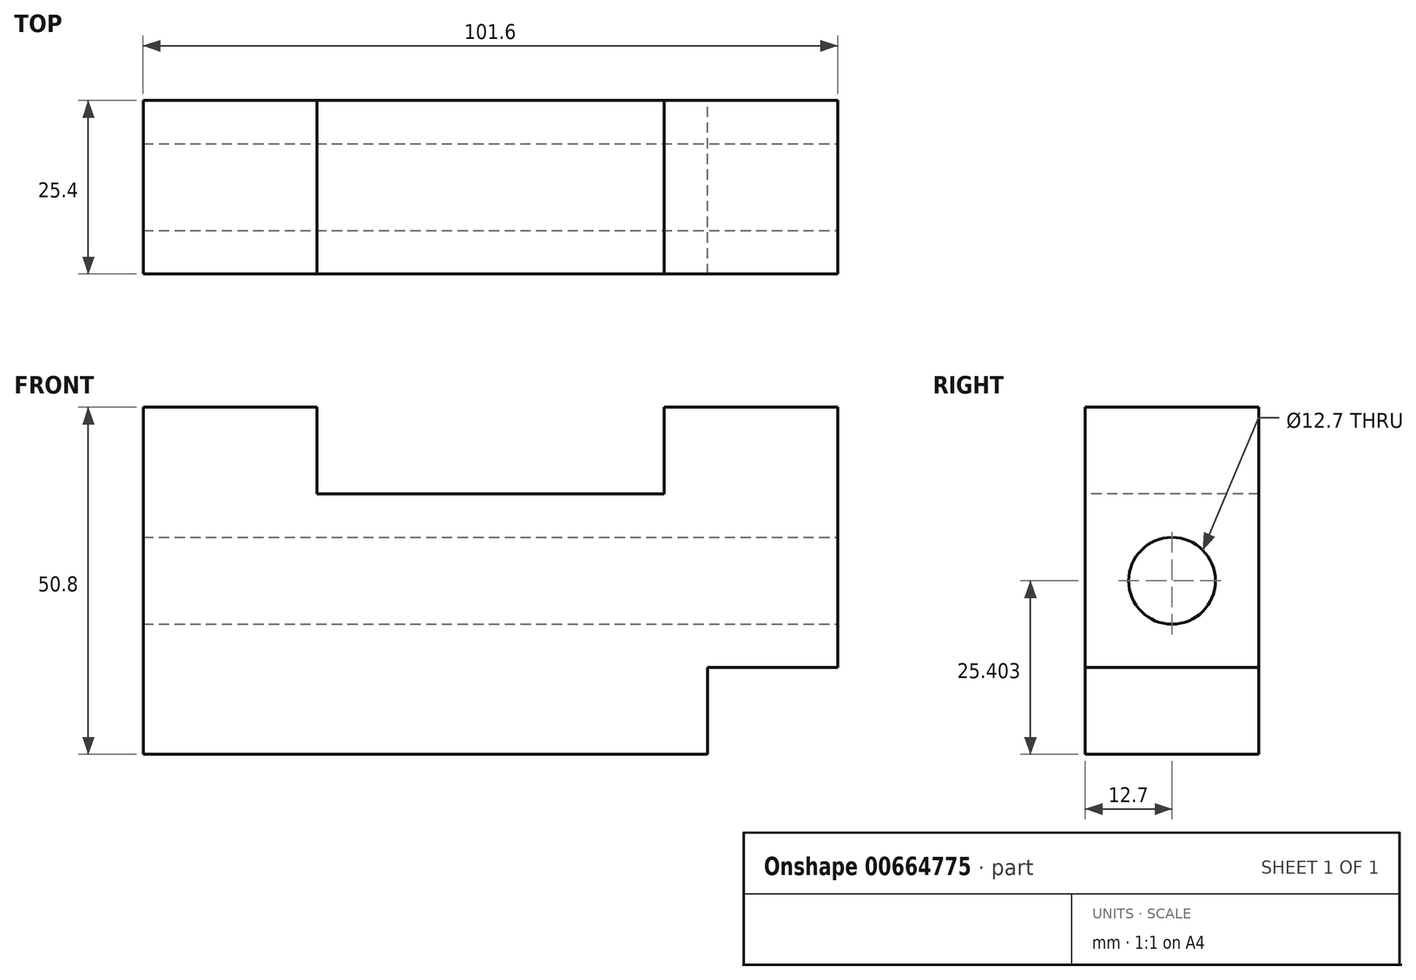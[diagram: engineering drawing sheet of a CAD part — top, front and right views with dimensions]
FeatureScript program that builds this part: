
annotation { "Feature Type Name" : "Feature", "Feature Type Description" : "" }
export const myFeature = defineFeature(function(context is Context, id is Id, definition is map)
    precondition{}
    {
        {
            var Q0;
            Q0=qCreatedBy(makeId("Front.planeOp"),FACE);
            var sketch = newSketch(context, id + "F0", { "sketchPlane" : qUnion([Q0])});
            skLineSegment(sketch, "E0.bottom", {"start": v(-52.56, 56.98) * mm, "end": v(49.04, 56.98) * mm});
            skLineSegment(sketch, "E0.top", {"start": v(-52.56, 6.18) * mm, "end": v(49.04, 6.18) * mm});
            skLineSegment(sketch, "E0.left", {"start": v(-52.56, 56.98) * mm, "end": v(-52.56, 6.18) * mm});
            skLineSegment(sketch, "E0.right", {"start": v(49.04, 56.98) * mm, "end": v(49.04, 6.18) * mm});
            skSolve(sketch);
        }
        {
            var Q0;
            Q0=makeQuery(id+"F0.imprint","IMPRINT",FACE,{"disambiguationData":[TD([[makeQuery(id+"F0.imprint","IMPRINT",EDGE,{"derivedFrom":sQuery(id+"F0.wireOp",EDGE,"E0.bottom")}),-1.0]])]});
            extrude(context, id + "F1", {"entities" : qUnion([Q0]), "depth" : 25.4 * mm, "offsetDistance" : 25.4 * mm});
        }
        {
            var Q0;
            Q0=makeQuery(id+"F1.opExtrude","CAP_FACE",FACE,{"disambiguationData":[OSD([sQuery(id+"F0.wireOp",EDGE,"E0.bottom"),sQuery(id+"F0.wireOp",EDGE,"E0.top"),sQuery(id+"F0.wireOp",EDGE,"E0.left"),sQuery(id+"F0.wireOp",EDGE,"E0.right")])],"isStart":false});
            var sketch = newSketch(context, id + "F2", { "sketchPlane" : qUnion([Q0])});
            skLineSegment(sketch, "E1.bottom", {"start": v(-27.16, 56.98) * mm, "end": v(23.64, 56.98) * mm});
            skLineSegment(sketch, "E1.top", {"start": v(-27.16, 44.28) * mm, "end": v(23.64, 44.28) * mm});
            skLineSegment(sketch, "E1.left", {"start": v(-27.16, 56.98) * mm, "end": v(-27.16, 44.28) * mm});
            skLineSegment(sketch, "E1.right", {"start": v(23.64, 56.98) * mm, "end": v(23.64, 44.28) * mm});
            skSolve(sketch);
        }
        {
            var Q0;
            Q0 = qSketchRegion(id + "F2", true);
            extrude(context, id + "F3", {"entities" : qUnion([Q0]), "operationType" : NewBodyOperationType.REMOVE, "oppositeDirection" : true, "depth" : 25.4 * mm, "offsetDistance" : 25.4 * mm});
        }
        {
            var Q0;
            Q0=makeQuery(id+"F1.opExtrude","SWEPT_FACE",FACE,{"disambiguationData":[OSD([sQuery(id+"F0.wireOp",EDGE,"E0.right")])]});
            var sketch = newSketch(context, id + "F4", { "sketchPlane" : qUnion([Q0])});
            skLineSegment(sketch, "E2.bottom", {"start": v(-25.4, 18.88) * mm, "end": v(0, 18.88) * mm});
            skLineSegment(sketch, "E2.top", {"start": v(-25.4, 6.18) * mm, "end": v(0, 6.18) * mm});
            skLineSegment(sketch, "E2.left", {"start": v(-25.4, 18.88) * mm, "end": v(-25.4, 6.18) * mm});
            skLineSegment(sketch, "E2.right", {"start": v(0, 18.88) * mm, "end": v(0, 6.18) * mm});
            skSolve(sketch);
        }
        {
            var Q0;
            Q0 = qSketchRegion(id + "F4", true);
            extrude(context, id + "F5", {"entities" : qUnion([Q0]), "operationType" : NewBodyOperationType.REMOVE, "oppositeDirection" : true, "depth" : 19.05 * mm, "offsetDistance" : 25.4 * mm});
        }
        {
            var Q0;
            Q0=makeQuery(id+"F1.opExtrude","SWEPT_FACE",FACE,{"disambiguationData":[OSD([sQuery(id+"F0.wireOp",EDGE,"E0.right")])]});
            var sketch = newSketch(context, id + "F6", { "sketchPlane" : qUnion([Q0])});
            skCircle(sketch, "E3", {"center": v(-12.7, 31.58) * mm, "radius": 6.35 * mm});
            skSolve(sketch);
        }
        {
            var Q0;
            Q0 = qSketchRegion(id + "F6", true);
            extrude(context, id + "F7", {"entities" : qUnion([Q0]), "operationType" : NewBodyOperationType.REMOVE, "endBound" : BoundingType.THROUGH_ALL, "oppositeDirection" : true, "depth" : 25.4 * mm, "offsetDistance" : 25.4 * mm});
        }
    });
